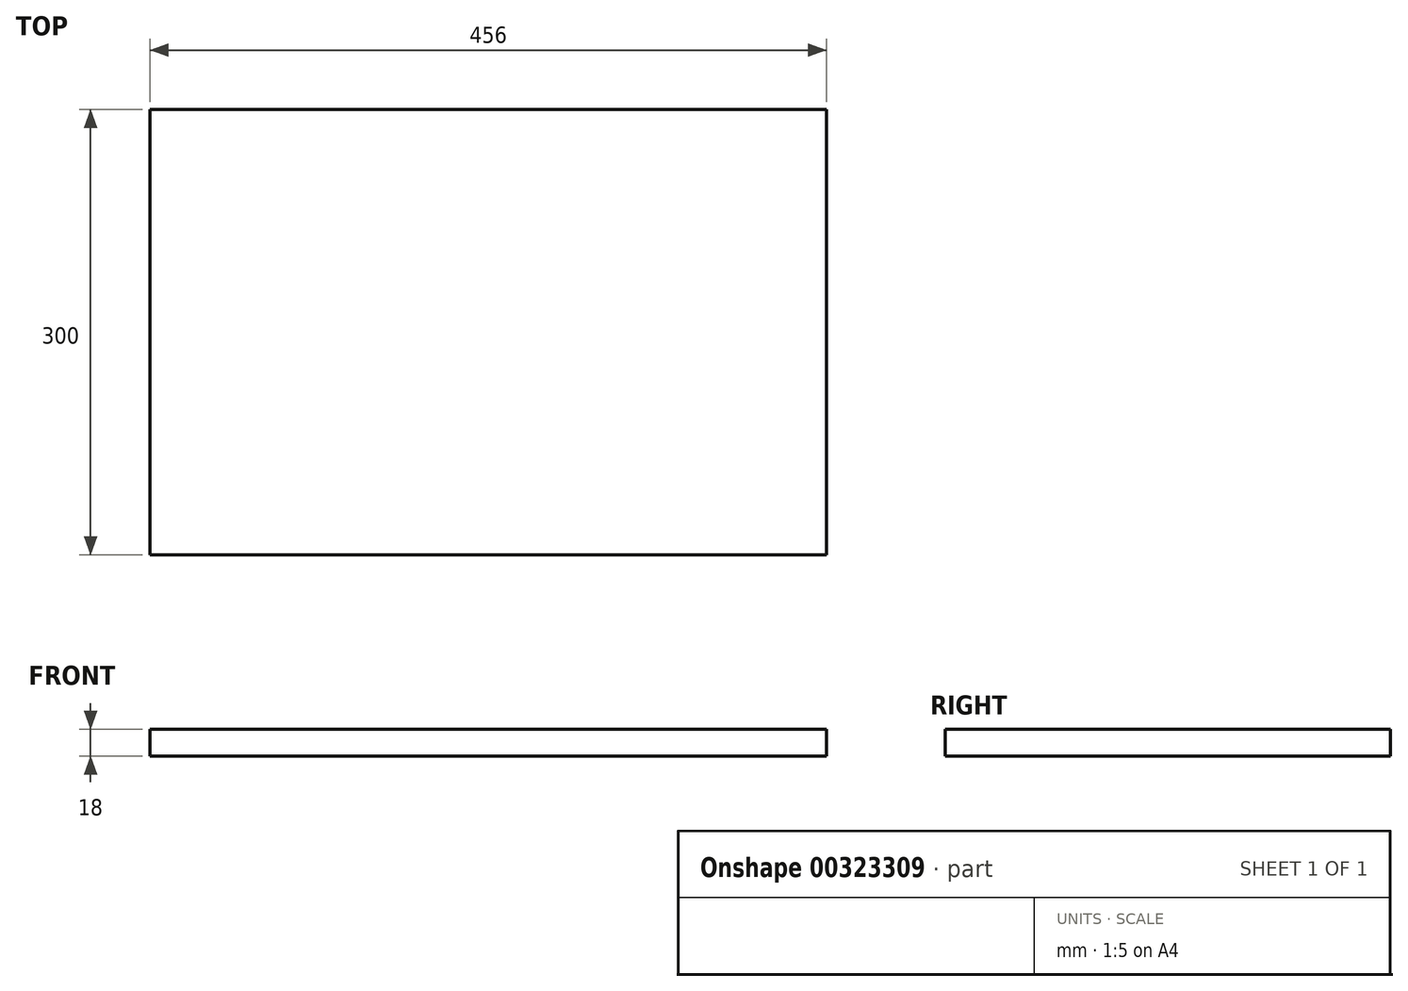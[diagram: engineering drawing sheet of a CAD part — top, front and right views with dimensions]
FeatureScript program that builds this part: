
annotation { "Feature Type Name" : "Feature", "Feature Type Description" : "" }
export const myFeature = defineFeature(function(context is Context, id is Id, definition is map)
    precondition{}
    {
        {
            var Q0;
            Q0=qCreatedBy(makeId("Top.planeOp"),FACE);
            var sketch = newSketch(context, id + "F0", { "sketchPlane" : qUnion([Q0])});
            skLineSegment(sketch, "E0.bottom", {"start": v(0, 0) * mm, "end": v(456, 0) * mm});
            skLineSegment(sketch, "E0.top", {"start": v(0, 300) * mm, "end": v(456, 300) * mm});
            skLineSegment(sketch, "E0.left", {"start": v(0, 0) * mm, "end": v(0, 300) * mm});
            skLineSegment(sketch, "E0.right", {"start": v(456, 0) * mm, "end": v(456, 300) * mm});
            skSolve(sketch);
        }
        {
            var Q0;
            Q0 = qSketchRegion(id + "F0", true);
            extrude(context, id + "F1", {"entities" : qUnion([Q0]), "depth" : 18 * mm, "offsetDistance" : 25 * mm});
        }
    });
